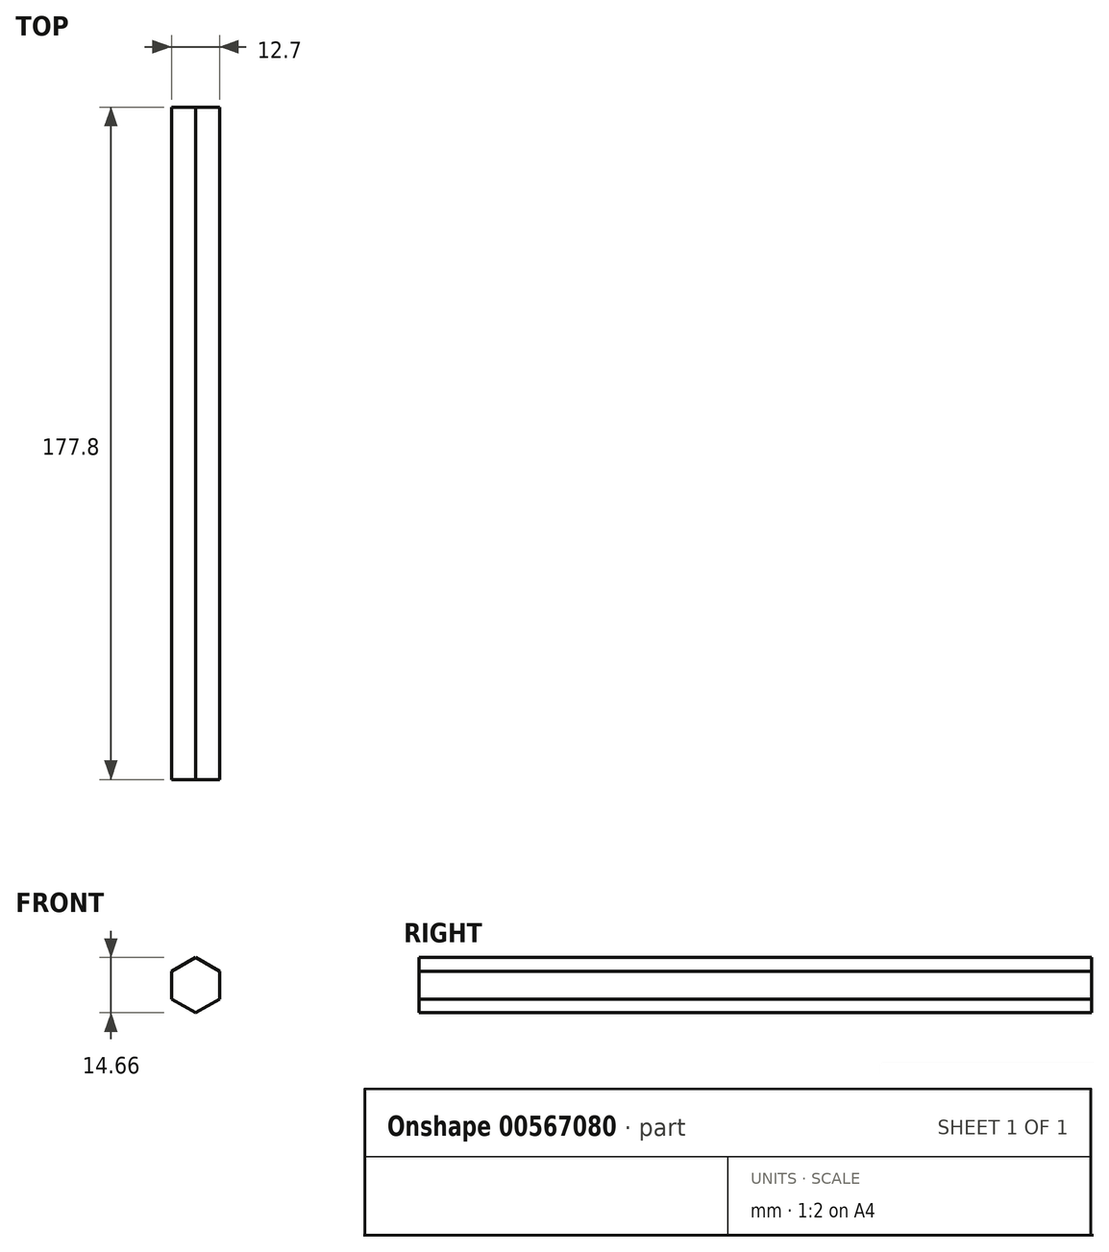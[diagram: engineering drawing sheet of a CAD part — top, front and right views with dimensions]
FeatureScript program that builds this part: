
annotation { "Feature Type Name" : "Feature", "Feature Type Description" : "" }
export const myFeature = defineFeature(function(context is Context, id is Id, definition is map)
    precondition{}
    {
        {
            var Q0;
            Q0=qCreatedBy(makeId("Front.planeOp"),FACE);
            var sketch = newSketch(context, id + "F0", { "sketchPlane" : qUnion([Q0])});
            skCircle(sketch, "E0.cCircle", {"center": v(0, 0) * mm, "radius": 6.35 * mm, "construction": true});
            skLineSegment(sketch, "E0.0", {"start": v(6.35, 3.67) * mm, "end": v(6.35, -3.67) * mm});
            skLineSegment(sketch, "E0.1", {"start": v(6.35, -3.67) * mm, "end": v(0, -7.33) * mm});
            skLineSegment(sketch, "E0.2", {"start": v(0, -7.33) * mm, "end": v(-6.35, -3.67) * mm});
            skLineSegment(sketch, "E0.3", {"start": v(-6.35, -3.67) * mm, "end": v(-6.35, 3.67) * mm});
            skLineSegment(sketch, "E0.4", {"start": v(-6.35, 3.67) * mm, "end": v(0, 7.33) * mm});
            skLineSegment(sketch, "E0.5", {"start": v(0, 7.33) * mm, "end": v(6.35, 3.67) * mm});
            skPoint(sketch, "E0.0.midPoint", {"position": v(6.35, 0) * mm});
            skSolve(sketch);
        }
        {
            var Q0;
            Q0=qSketchRegion(id+"F0",true);
            extrude(context, id + "F1", {"entities" : qUnion([Q0]), "depth" : 177.8 * mm});
        }
    });
